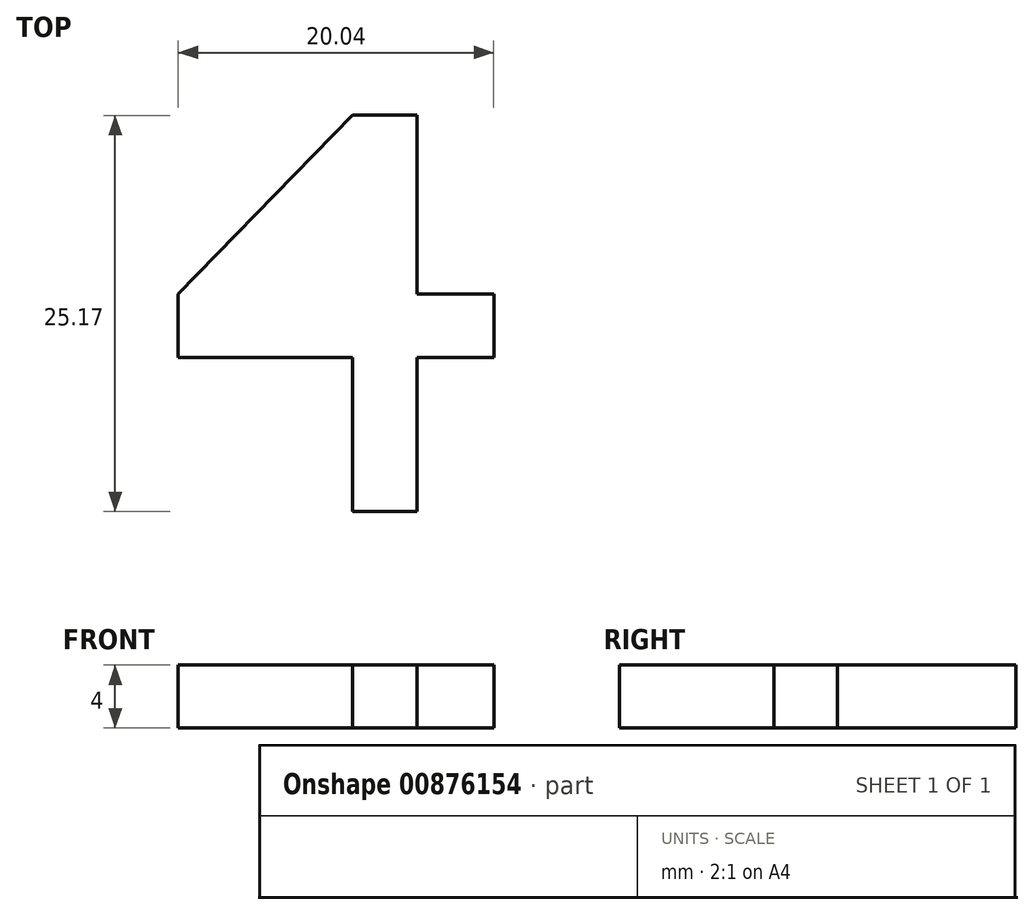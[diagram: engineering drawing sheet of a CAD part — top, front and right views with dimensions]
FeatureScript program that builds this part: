
annotation { "Feature Type Name" : "Feature", "Feature Type Description" : "" }
export const myFeature = defineFeature(function(context is Context, id is Id, definition is map)
    precondition{}
    {
        {
            var Q0;
            Q0=qCreatedBy(makeId("Top.planeOp"),FACE);
            var sketch = newSketch(context, id + "F0", { "sketchPlane" : qUnion([Q0])});
            skLineSegment(sketch, "E0", {"start": v(0, 0) * mm, "end": v(0, 9.79) * mm});
            skLineSegment(sketch, "E1", {"start": v(0, 9.79) * mm, "end": v(-11.08, 9.79) * mm});
            skLineSegment(sketch, "E2", {"start": v(-11.08, 9.79) * mm, "end": v(-11.08, 13.84) * mm});
            skLineSegment(sketch, "E3", {"start": v(-11.08, 13.84) * mm, "end": v(0, 25.17) * mm});
            skLineSegment(sketch, "E4", {"start": v(0, 25.17) * mm, "end": v(4.1, 25.17) * mm});
            skLineSegment(sketch, "E5", {"start": v(4.1, 25.17) * mm, "end": v(4.1, 13.84) * mm});
            skLineSegment(sketch, "E6", {"start": v(4.1, 13.84) * mm, "end": v(8.96, 13.84) * mm});
            skLineSegment(sketch, "E7", {"start": v(8.96, 13.84) * mm, "end": v(8.96, 9.79) * mm});
            skLineSegment(sketch, "E8", {"start": v(8.96, 9.79) * mm, "end": v(4.1, 9.79) * mm});
            skLineSegment(sketch, "E9", {"start": v(4.1, 9.79) * mm, "end": v(4.1, 0) * mm});
            skLineSegment(sketch, "E10", {"start": v(4.1, 0) * mm, "end": v(0, 0) * mm});
            skSolve(sketch);
        }
        {
            var Q0;
            Q0=makeQuery(id+"F0.imprint","IMPRINT",FACE,{"disambiguationData":[TD([[makeQuery(id+"F0.imprint","IMPRINT",EDGE,{"derivedFrom":sQuery(id+"F0.wireOp",EDGE,"E0")}),-1.0]])]});
            extrude(context, id + "F1", {"entities" : qUnion([Q0]), "depth" : 4 * mm, "offsetDistance" : 25 * mm});
        }
    });
